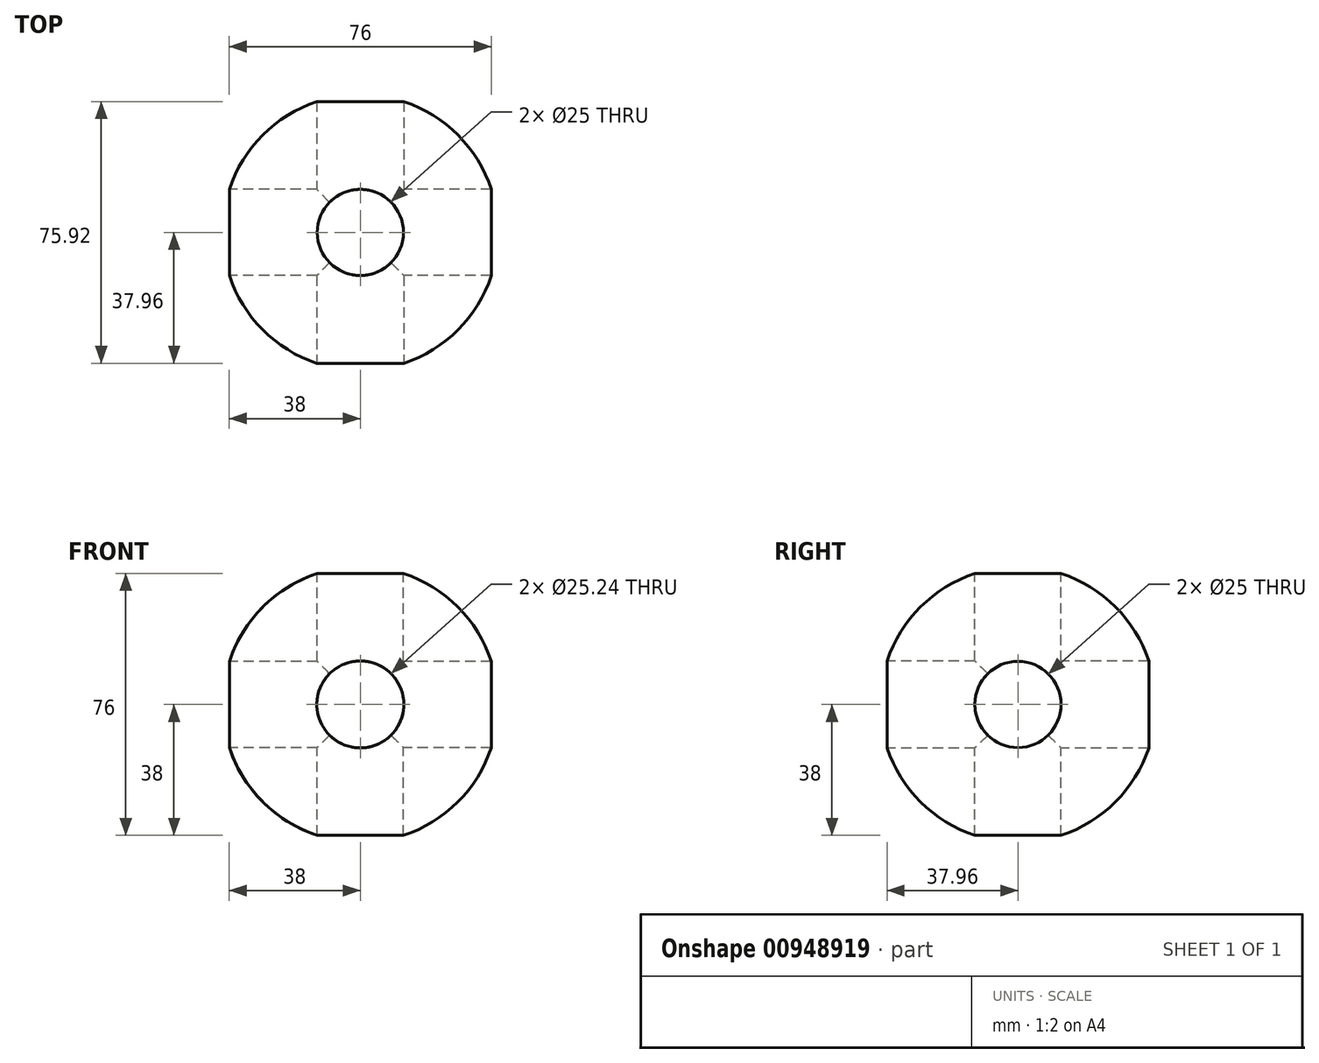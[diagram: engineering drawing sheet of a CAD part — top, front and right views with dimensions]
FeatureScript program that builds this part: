
annotation { "Feature Type Name" : "Feature", "Feature Type Description" : "" }
export const myFeature = defineFeature(function(context is Context, id is Id, definition is map)
    precondition{}
    {
        {
            var Q0;
            Q0=qCreatedBy(makeId("Front.planeOp"),FACE);
            var sketch = newSketch(context, id + "F0", { "sketchPlane" : qUnion([Q0])});
            skArc(sketch, "E0", {"start": v(0, -40) * mm, "mid": v(40, 0) * mm, "end": v(0, 40) * mm});
            skLineSegment(sketch, "E1", {"start": v(0, 40) * mm, "end": v(0, -40) * mm});
            skSolve(sketch);
        }
        {
            var Q0;
            Q0=makeQuery(id+"F0.imprint","IMPRINT",FACE,{"disambiguationData":[TD([[makeQuery(id+"F0.imprint","IMPRINT",EDGE,{"derivedFrom":sQuery(id+"F0.wireOp",EDGE,"E0")}),1.0]])]});
            var Q1;
            Q1=sQuery(id+"F0.wireOp",EDGE,"E1");
            revolve(context, id + "F1", {"surfaceOperationType" : NewSurfaceOperationType.NEW, "entities" : qUnion([Q0]), "axis" : qUnion([Q1]), "revolveType" : RevolveType.FULL});
        }
        {
            var Q0;
            Q0=qCreatedBy(makeId("Right.planeOp"),FACE);
            var sketch = newSketch(context, id + "F2", { "sketchPlane" : qUnion([Q0])});
            skCircle(sketch, "E2", {"center": v(0, 0) * mm, "radius": 12.5 * mm});
            skSolve(sketch);
        }
        {
            var Q0;
            Q0 = qSketchRegion(id + "F2", true);
            extrude(context, id + "F3", {"entities" : qUnion([Q0]), "operationType" : NewBodyOperationType.REMOVE, "endBound" : BoundingType.SYMMETRIC, "depth" : 80 * mm, "offsetDistance" : 25.4 * mm});
        }
        {
            var Q0;
            Q0=qCreatedBy(makeId("Front.planeOp"),FACE);
            var sketch = newSketch(context, id + "F4", { "sketchPlane" : qUnion([Q0])});
            skCircle(sketch, "E3", {"center": v(0, 0) * mm, "radius": 12.62 * mm});
            skSolve(sketch);
        }
        {
            var Q0;
            Q0 = qSketchRegion(id + "F4", true);
            extrude(context, id + "F5", {"entities" : qUnion([Q0]), "operationType" : NewBodyOperationType.REMOVE, "endBound" : BoundingType.SYMMETRIC, "oppositeDirection" : true, "depth" : 80 * mm, "offsetDistance" : 25.4 * mm});
        }
        {
            var Q0;
            Q0=qCreatedBy(makeId("Top.planeOp"),FACE);
            var sketch = newSketch(context, id + "F6", { "sketchPlane" : qUnion([Q0])});
            skCircle(sketch, "E4", {"center": v(0, 0) * mm, "radius": 12.5 * mm});
            skSolve(sketch);
        }
        {
            var Q0;
            Q0 = qSketchRegion(id + "F6", true);
            extrude(context, id + "F7", {"entities" : qUnion([Q0]), "operationType" : NewBodyOperationType.REMOVE, "endBound" : BoundingType.SYMMETRIC, "oppositeDirection" : true, "depth" : 80 * mm, "offsetDistance" : 25.4 * mm});
        }
    });
